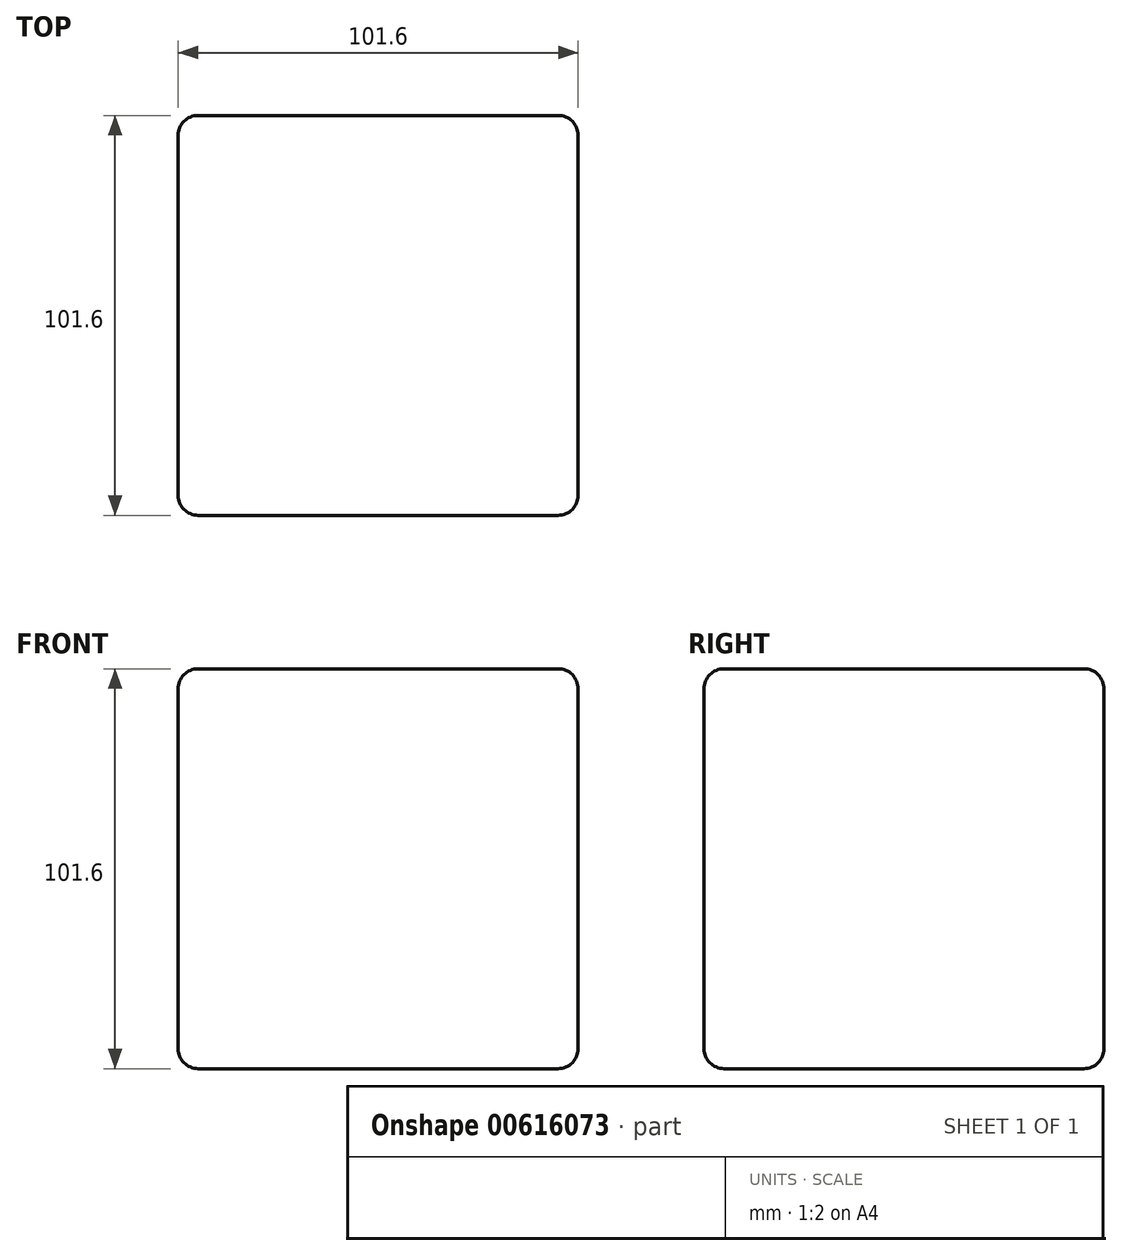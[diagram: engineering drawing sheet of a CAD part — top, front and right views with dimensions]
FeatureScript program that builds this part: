
annotation { "Feature Type Name" : "Feature", "Feature Type Description" : "" }
export const myFeature = defineFeature(function(context is Context, id is Id, definition is map)
    precondition{}
    {
        {
            var Q0;
            Q0=qCreatedBy(makeId("Top.planeOp"),FACE);
            var sketch = newSketch(context, id + "F0", { "sketchPlane" : qUnion([Q0])});
            skLineSegment(sketch, "E0.bottom", {"start": v(-56.84, 53.4) * mm, "end": v(44.76, 53.4) * mm});
            skLineSegment(sketch, "E0.top", {"start": v(-56.84, -48.2) * mm, "end": v(44.76, -48.2) * mm});
            skLineSegment(sketch, "E0.left", {"start": v(-56.84, 53.4) * mm, "end": v(-56.84, -48.2) * mm});
            skLineSegment(sketch, "E0.right", {"start": v(44.76, 53.4) * mm, "end": v(44.76, -48.2) * mm});
            skSolve(sketch);
        }
        {
            var Q0;
            Q0=makeQuery(id+"F0.imprint","IMPRINT",FACE,{"disambiguationData":[TD([[makeQuery(id+"F0.imprint","IMPRINT",EDGE,{"derivedFrom":sQuery(id+"F0.wireOp",EDGE,"E0.bottom")}),-1.0]])]});
            extrude(context, id + "F1", {"entities" : qUnion([Q0]), "depth" : 101.6 * mm, "offsetDistance" : 25.4 * mm});
        }
        {
            var Q0;
            Q0=makeQuery(id+"F1.opExtrude","CAP_EDGE",EDGE,{"disambiguationData":[OSD([sQuery(id+"F0.wireOp",EDGE,"E0.top")])],"isStart":false});
            var Q1;
            Q1=makeQuery(id+"F1.opExtrude","CAP_EDGE",EDGE,{"disambiguationData":[OSD([sQuery(id+"F0.wireOp",EDGE,"E0.right")])],"isStart":false});
            var Q2;
            Q2=makeQuery(id+"F1.opExtrude","CAP_EDGE",EDGE,{"disambiguationData":[OSD([sQuery(id+"F0.wireOp",EDGE,"E0.bottom")])],"isStart":false});
            var Q3;
            Q3=makeQuery(id+"F1.opExtrude","CAP_EDGE",EDGE,{"disambiguationData":[OSD([sQuery(id+"F0.wireOp",EDGE,"E0.left")])],"isStart":false});
            var Q4;
            Q4=makeQuery(id+"F1.opExtrude","SWEPT_FACE",FACE,{"disambiguationData":[OSD([sQuery(id+"F0.wireOp",EDGE,"E0.top")])]});
            var Q5;
            Q5=makeQuery(id+"F1.opExtrude","SWEPT_EDGE",EDGE,{"disambiguationData":[OSD([sQuery(id+"F0.wireOp",EDGE,"E0.bottom"),sQuery(id+"F0.wireOp",EDGE,"E0.right")])]});
            var Q6;
            Q6=makeQuery(id+"F1.opExtrude","CAP_EDGE",EDGE,{"disambiguationData":[OSD([sQuery(id+"F0.wireOp",EDGE,"E0.right")])],"isStart":true});
            var Q7;
            Q7=makeQuery(id+"F1.opExtrude","CAP_EDGE",EDGE,{"disambiguationData":[OSD([sQuery(id+"F0.wireOp",EDGE,"E0.bottom")])],"isStart":true});
            var Q8;
            Q8=makeQuery(id+"F1.opExtrude","SWEPT_EDGE",EDGE,{"disambiguationData":[OSD([sQuery(id+"F0.wireOp",EDGE,"E0.bottom"),sQuery(id+"F0.wireOp",EDGE,"E0.left")])]});
            var Q9;
            Q9=makeQuery(id+"F1.opExtrude","CAP_EDGE",EDGE,{"disambiguationData":[OSD([sQuery(id+"F0.wireOp",EDGE,"E0.left")])],"isStart":true});
            fillet(context, id + "F2", {"entities" : qUnion([Q0, Q1, Q2, Q3, Q4, Q5, Q6, Q7, Q8, Q9]), "radius" : 5.08 * mm, "tangentPropagation" : true, "allowEdgeOverflow" : false});
        }
    });
